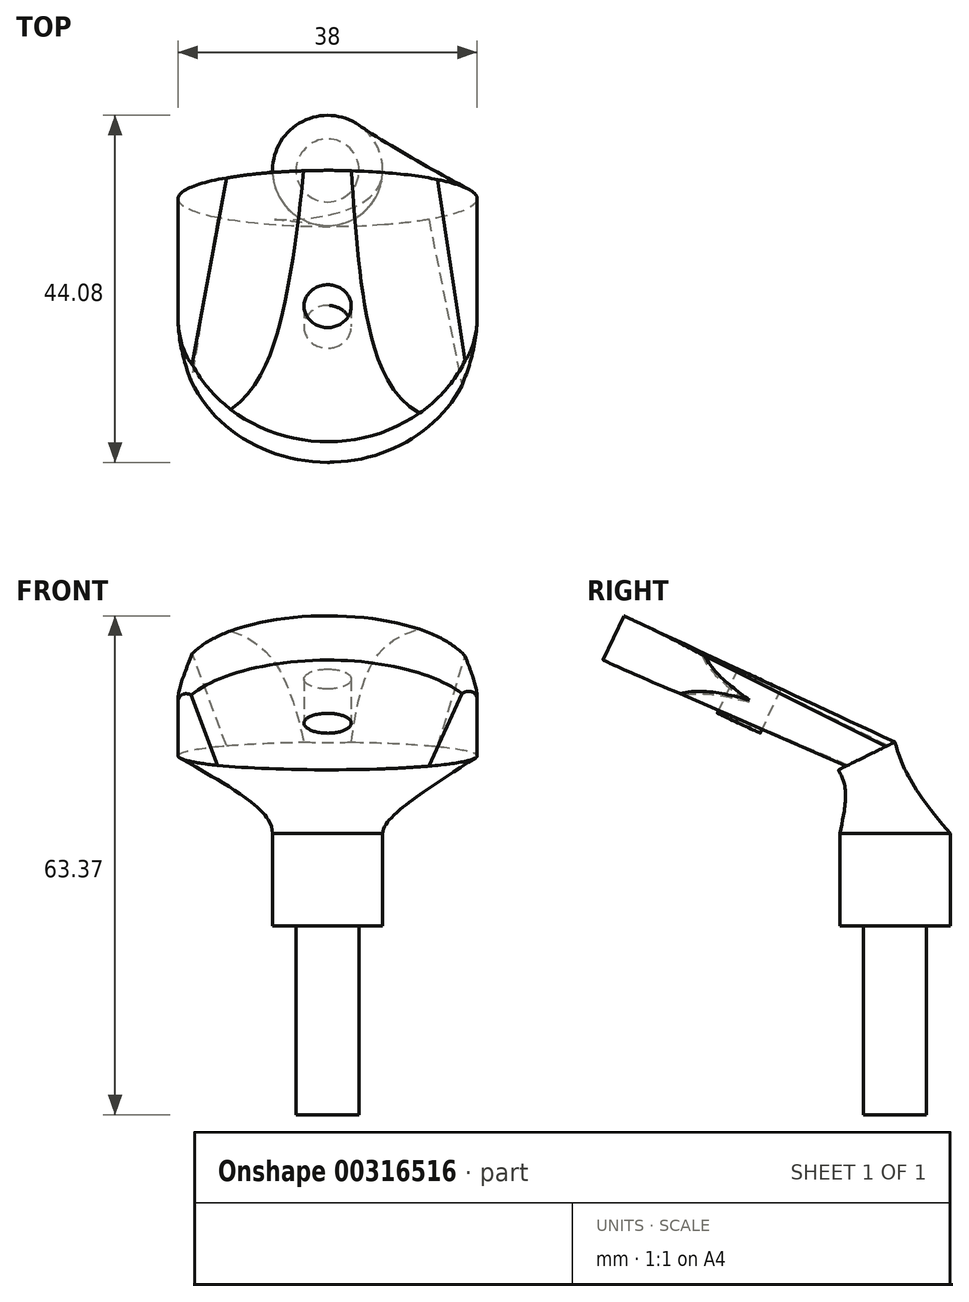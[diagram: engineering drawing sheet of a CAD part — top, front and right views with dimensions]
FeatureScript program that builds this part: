
annotation { "Feature Type Name" : "Feature", "Feature Type Description" : "" }
export const myFeature = defineFeature(function(context is Context, id is Id, definition is map)
    precondition{}
    {
        {
            var Q0;
            Q0=qCreatedBy(makeId("Top.planeOp"),FACE);
            var sketch = newSketch(context, id + "F0", { "sketchPlane" : qUnion([Q0])});
            skCircle(sketch, "E0", {"center": v(0, 0) * mm, "radius": 7 * mm});
            skSolve(sketch);
        }
        {
            var Q0;
            Q0=makeQuery(id+"F0.imprint","IMPRINT",FACE,{"disambiguationData":[TD([[makeQuery(id+"F0.imprint","IMPRINT",EDGE,{"derivedFrom":sQuery(id+"F0.wireOp",EDGE,"E0")}),1.0]])]});
            extrude(context, id + "F1", {"entities" : qUnion([Q0]), "depth" : 11.75 * mm});
        }
        {
            var Q0;
            Q0=makeQuery(id+"F1.opExtrude","CAP_FACE",FACE,{"disambiguationData":[OSD([sQuery(id+"F0.wireOp",EDGE,"E0")])],"isStart":false});
            var sketch = newSketch(context, id + "F2", { "sketchPlane" : qUnion([Q0])});
            skCircle(sketch, "E1", {"center": v(0, 0) * mm, "radius": 7 * mm});
            skSolve(sketch);
        }
        {
            var Q0;
            Q0=makeQuery(id+"F2.imprint","IMPRINT",FACE,{"disambiguationData":[TD([[makeQuery(id+"F2.imprint","IMPRINT",EDGE,{"derivedFrom":sQuery(id+"F2.wireOp",EDGE,"E1")}),1.0]])]});
            cPlane(context, id + "F3", {"entities" : qUnion([Q0]), "cplaneType" : CPlaneType.OFFSET, "offset" : 11.6 * mm, "width" : 150 * mm, "height" : 150 * mm});
        }
        {
            var Q0;
            Q0=qCreatedBy(id+"F3.planeOp",FACE);
            var sketch = newSketch(context, id + "F4", { "sketchPlane" : qUnion([Q0])});
            skLineSegment(sketch, "E2", {"start": v(-7.89, 0) * mm, "end": v(8.5, 0) * mm, "construction": true});
            skSolve(sketch);
        }
        {
            var Q0;
            Q0=qCreatedBy(id+"F3.planeOp",FACE);
            var Q1;
            Q1=sQuery(id+"F4.wireOp",EDGE,"E2");
            cPlane(context, id + "F5", {"entities" : qUnion([Q0, Q1]), "cplaneType" : CPlaneType.LINE_ANGLE, "offset" : 25 * mm, "angle" : 26.26 * degree, "width" : 150 * mm, "height" : 150 * mm});
        }
        {
            var Q0;
            Q0=qCreatedBy(id+"F5.planeOp",FACE);
            var sketch = newSketch(context, id + "F6", { "sketchPlane" : qUnion([Q0])});
            skEllipse(sketch, "E3", {"center": v(0, -6.33) * mm, "majorRadius": 19 * mm, "minorRadius": 4 * mm, "majorAxis": v(-1, 0)});
            skSolve(sketch);
        }
        {
            var Q0;
            Q0=makeQuery(id+"F2.imprint","IMPRINT",FACE,{"disambiguationData":[TD([[makeQuery(id+"F2.imprint","IMPRINT",EDGE,{"derivedFrom":sQuery(id+"F2.wireOp",EDGE,"E1")}),1.0]])]});
            var Q1;
            Q1=makeQuery(id+"F6.imprint","IMPRINT",FACE,{"disambiguationData":[TD([[makeQuery(id+"F6.imprint","IMPRINT",EDGE,{"derivedFrom":sQuery(id+"F6.wireOp",EDGE,"E3")}),1.0]])]});
            loft(context, id + "F7", {"sheetProfilesArray" : [{ "sheetProfileEntities" : qUnion([Q0]) }, { "sheetProfileEntities" : qUnion([Q1]) }]});
        }
        {
            var Q0;
            Q0=qCreatedBy(id+"F5.planeOp",FACE);
            var Q1;
            Q1=sQuery(id+"F4.wireOp",EDGE,"E2");
            cPlane(context, id + "F8", {"entities" : qUnion([Q0, Q1]), "cplaneType" : CPlaneType.LINE_ANGLE, "offset" : 25 * mm, "angle" : 38.74 * degree, "width" : 150 * mm, "height" : 150 * mm});
        }
        {
            var Q0;
            Q0=qCreatedBy(id+"F8.planeOp",FACE);
            cPlane(context, id + "F9", {"entities" : qUnion([Q0]), "cplaneType" : CPlaneType.OFFSET, "offset" : 38 * mm, "width" : 150 * mm, "height" : 150 * mm});
        }
        {
            var Q0;
            Q0=qCreatedBy(id+"F9.planeOp",FACE);
            var sketch = newSketch(context, id + "F10", { "sketchPlane" : qUnion([Q0])});
            skLineSegment(sketch, "E4.bottom", {"start": v(-19, 14.92) * mm, "end": v(19, 14.92) * mm});
            skLineSegment(sketch, "E4.top", {"start": v(-19, 21.16) * mm, "end": v(19, 21.16) * mm});
            skLineSegment(sketch, "E4.left", {"start": v(-19, 14.92) * mm, "end": v(-19, 21.16) * mm});
            skLineSegment(sketch, "E4.right", {"start": v(19, 14.92) * mm, "end": v(19, 21.16) * mm});
            skSolve(sketch);
        }
        {
            var Q1;
            Q1=makeQuery(id+"F7.opLoft","CAP_FACE",FACE,{"disambiguationData":[OSD([makeQuery(id+"F6.imprint","IMPRINT",FACE,{"disambiguationData":[TD([[makeQuery(id+"F6.imprint","IMPRINT",EDGE,{"derivedFrom":sQuery(id+"F6.wireOp",EDGE,"E3")}),1.0]])]})])],"isStart":true});
            var Q2;
            Q2=makeQuery(id+"F10.imprint","IMPRINT",FACE,{"disambiguationData":[TD([[makeQuery(id+"F10.imprint","IMPRINT",EDGE,{"derivedFrom":sQuery(id+"F10.wireOp",EDGE,"E4.bottom")}),1.0]])]});
            loft(context, id + "F11", {"operationType" : NewBodyOperationType.ADD, "sheetProfilesArray" : [{ "sheetProfileEntities" : qUnion([Q1]) }, { "sheetProfileEntities" : qUnion([Q2]) }]});
        }
        {
            var Q0;
            Q0=qCreatedBy(id+"F9.planeOp",FACE);
            var Q1;
            Q1=makeQuery(id+"F11.opLoft","MID_CAP_EDGE",EDGE,{"disambiguationData":[OSD([sQuery(id+"F10.wireOp",EDGE,"E4.bottom"),sQuery(id+"F10.wireOp",EDGE,"E4.left"),sQuery(id+"F10.wireOp",EDGE,"E4.right")])],"capPos":1.0});
            cPlane(context, id + "F12", {"entities" : qUnion([Q0, Q1]), "cplaneType" : CPlaneType.LINE_ANGLE, "offset" : 25 * mm, "angle" : 90 * degree, "width" : 150 * mm, "height" : 150 * mm});
        }
        {
            var Q0;
            Q0=qCreatedBy(id+"F12.planeOp",FACE);
            var sketch = newSketch(context, id + "F13", { "sketchPlane" : qUnion([Q0])});
            skArc(sketch, "E5", {"start": v(-19, -28.87) * mm, "mid": v(0, -47.87) * mm, "end": v(19, -28.87) * mm});
            skLineSegment(sketch, "E6", {"start": v(-19, -28.87) * mm, "end": v(19, -28.87) * mm});
            skLineSegment(sketch, "E7", {"start": v(-19, -28.87) * mm, "end": v(-19, -47.87) * mm});
            skLineSegment(sketch, "E8", {"start": v(-19, -47.87) * mm, "end": v(19, -47.87) * mm});
            skLineSegment(sketch, "E9", {"start": v(19, -47.87) * mm, "end": v(19, -28.87) * mm});
            skSolve(sketch);
        }
        {
            var Q0;
            {var subQ0=sQuery(id+"F13.wireOp",EDGE,"E7");Q0=makeQuery(id+"F13.imprint","IMPRINT",FACE,{"disambiguationData":[TD([[makeQuery(id+"F13.imprint","IMPRINT",EDGE,{"derivedFrom":subQ0}),1.0]])]});}
            var Q1;
            {var subQ0=sQuery(id+"F13.wireOp",EDGE,"E9");Q1=makeQuery(id+"F13.imprint","IMPRINT",FACE,{"disambiguationData":[TD([[makeQuery(id+"F13.imprint","IMPRINT",EDGE,{"derivedFrom":subQ0}),1.0]])]});}
            extrude(context, id + "F14", {"entities" : qUnion([Q0, Q1]), "operationType" : NewBodyOperationType.REMOVE, "depth" : 25 * mm});
        }
        {
            var Q0;
            Q0=qCreatedBy(id+"F12.planeOp",FACE);
            var sketch = newSketch(context, id + "F15", { "sketchPlane" : qUnion([Q0])});
            skArc(sketch, "E10.0", {"start": v(17.45, -36.38) * mm, "mid": v(0.3, -47.87) * mm, "end": v(-17.2, -36.93) * mm});
            skCircle(sketch, "E11", {"center": v(0, -28.87) * mm, "radius": 3 * mm});
            skSolve(sketch);
        }
        {
            var Q0;
            Q0 = qSketchRegion(id + "F15", true);
            extrude(context, id + "F16", {"entities" : qUnion([Q0]), "operationType" : NewBodyOperationType.REMOVE, "depth" : 25 * mm});
        }
        {
            var Q0;
            Q0=makeQuery(id+"F1.opExtrude","CAP_FACE",FACE,{"disambiguationData":[OSD([sQuery(id+"F0.wireOp",EDGE,"E0")])],"isStart":true});
            var sketch = newSketch(context, id + "F17", { "sketchPlane" : qUnion([Q0])});
            skCircle(sketch, "E12", {"center": v(0, 0) * mm, "radius": 4 * mm});
            skSolve(sketch);
        }
        {
            var Q0;
            Q0=makeQuery(id+"F17.imprint","IMPRINT",FACE,{"disambiguationData":[TD([[makeQuery(id+"F17.imprint","IMPRINT",EDGE,{"derivedFrom":sQuery(id+"F17.wireOp",EDGE,"E12")}),1.0]])]});
            extrude(context, id + "F18", {"entities" : qUnion([Q0]), "operationType" : NewBodyOperationType.ADD, "depth" : 24 * mm});
        }
        {
            var Q0;
            Q0=qCreatedBy(id+"F12.planeOp",FACE);
            cPlane(context, id + "F19", {"entities" : qUnion([Q0]), "cplaneType" : CPlaneType.OFFSET, "offset" : 6.2 * mm, "width" : 150 * mm, "height" : 150 * mm});
        }
        {
            var Q0;
            Q0=qCreatedBy(id+"F19.planeOp",FACE);
            var sketch = newSketch(context, id + "F20", { "sketchPlane" : qUnion([Q0])});
            skLineSegment(sketch, "E13.bottom", {"start": v(32.85, -3.44) * mm, "end": v(-32.85, -3.44) * mm});
            skLineSegment(sketch, "E13.top", {"start": v(32.85, -53.54) * mm, "end": v(-32.85, -53.54) * mm});
            skLineSegment(sketch, "E13.left", {"start": v(32.85, -3.44) * mm, "end": v(32.85, -53.54) * mm});
            skLineSegment(sketch, "E13.right", {"start": v(-32.85, -3.44) * mm, "end": v(-32.85, -53.54) * mm});
            skPoint(sketch, "E13.middle", {"position": v(0, -28.5) * mm});
            skSolve(sketch);
        }
        {
            var Q0;
            Q0=makeQuery(id+"F20.imprint","IMPRINT",FACE,{"disambiguationData":[TD([[makeQuery(id+"F20.imprint","IMPRINT",EDGE,{"derivedFrom":sQuery(id+"F20.wireOp",EDGE,"E13.bottom")}),1.0]])]});
            extrude(context, id + "F21", {"entities" : qUnion([Q0]), "operationType" : NewBodyOperationType.REMOVE, "depth" : 25 * mm});
        }
    });
